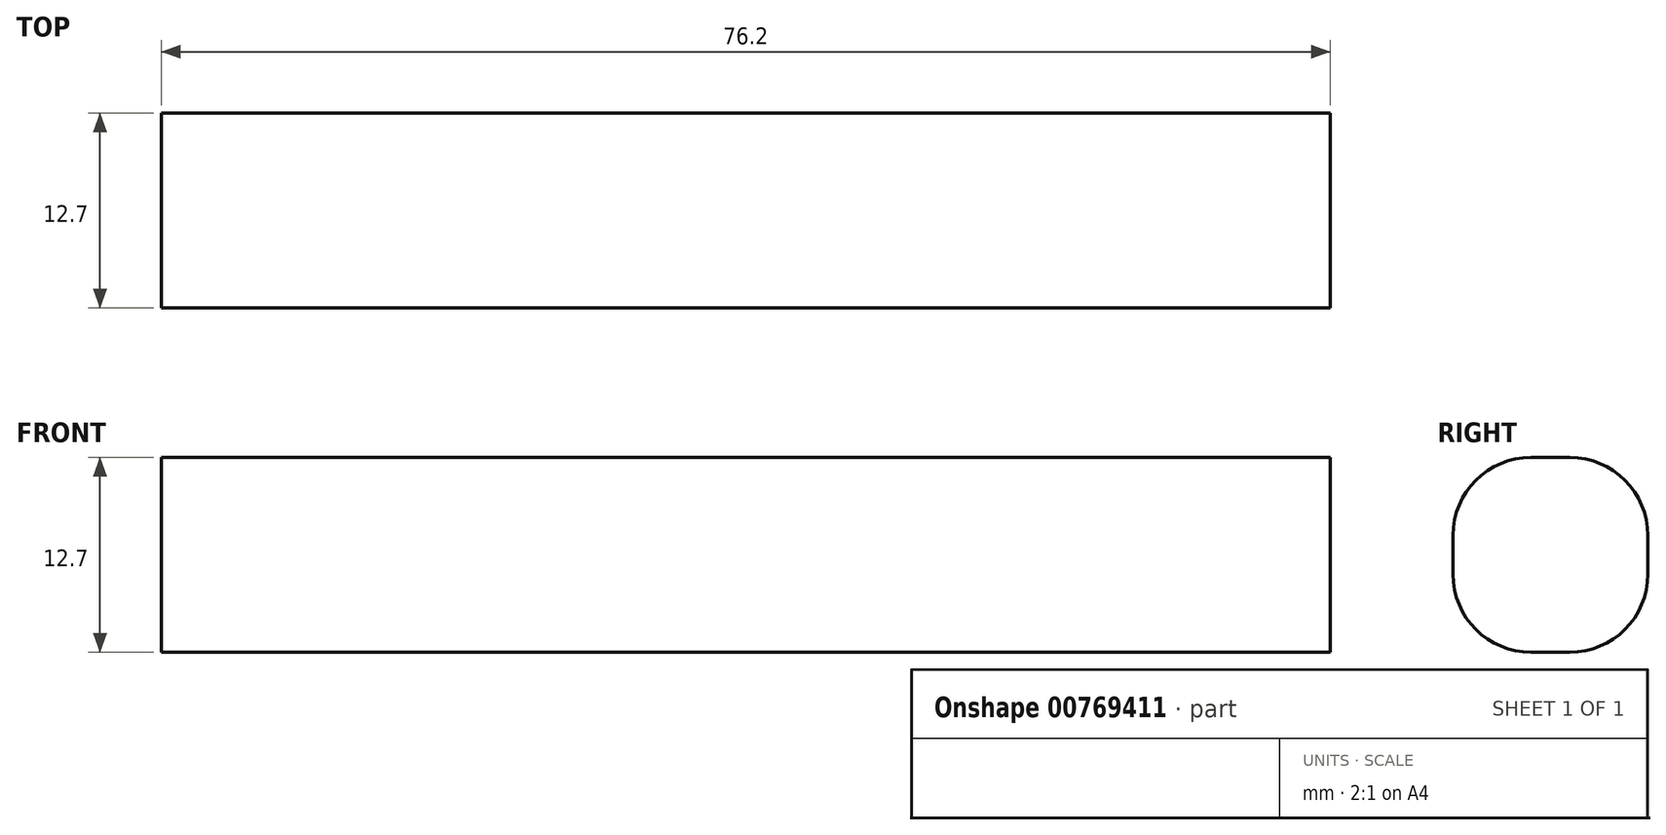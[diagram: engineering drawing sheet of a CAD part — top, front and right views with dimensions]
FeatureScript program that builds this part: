
annotation { "Feature Type Name" : "Feature", "Feature Type Description" : "" }
export const myFeature = defineFeature(function(context is Context, id is Id, definition is map)
    precondition{}
    {
        {
            var Q0;
            Q0=qCreatedBy(makeId("Top.planeOp"),FACE);
            var sketch = newSketch(context, id + "F0", { "sketchPlane" : qUnion([Q0])});
            skLineSegment(sketch, "E0.bottom", {"start": v(38.1, -6.35) * mm, "end": v(-38.1, -6.35) * mm});
            skLineSegment(sketch, "E0.top", {"start": v(38.1, 6.35) * mm, "end": v(-38.1, 6.35) * mm});
            skLineSegment(sketch, "E0.left", {"start": v(38.1, -6.35) * mm, "end": v(38.1, 6.35) * mm});
            skLineSegment(sketch, "E0.right", {"start": v(-38.1, -6.35) * mm, "end": v(-38.1, 6.35) * mm});
            skPoint(sketch, "E0.middle", {"position": v(0, 0) * mm});
            skSolve(sketch);
        }
        {
            var Q0;
            Q0=makeQuery(id+"F0.imprint","IMPRINT",FACE,{"disambiguationData":[TD([[makeQuery(id+"F0.imprint","IMPRINT",EDGE,{"derivedFrom":sQuery(id+"F0.wireOp",EDGE,"E0.bottom")}),-1.0]])]});
            extrude(context, id + "F1", {"entities" : qUnion([Q0]), "depth" : 12.7 * mm, "offsetDistance" : 25.4 * mm});
        }
        {
            var Q0;
            Q0=makeQuery(id+"F1.opExtrude","CAP_EDGE",EDGE,{"disambiguationData":[OSD([sQuery(id+"F0.wireOp",EDGE,"E0.bottom")])],"isStart":false});
            var Q1;
            Q1=makeQuery(id+"F1.opExtrude","CAP_EDGE",EDGE,{"disambiguationData":[OSD([sQuery(id+"F0.wireOp",EDGE,"E0.top")])],"isStart":false});
            var Q2;
            Q2=makeQuery(id+"F1.opExtrude","CAP_EDGE",EDGE,{"disambiguationData":[OSD([sQuery(id+"F0.wireOp",EDGE,"E0.bottom")])],"isStart":true});
            var Q3;
            Q3=makeQuery(id+"F1.opExtrude","CAP_EDGE",EDGE,{"disambiguationData":[OSD([sQuery(id+"F0.wireOp",EDGE,"E0.top")])],"isStart":true});
            fillet(context, id + "F2", {"entities" : qUnion([Q0, Q1, Q2, Q3]), "radius" : 5.08 * mm, "tangentPropagation" : true, "allowEdgeOverflow" : false});
        }
    });
